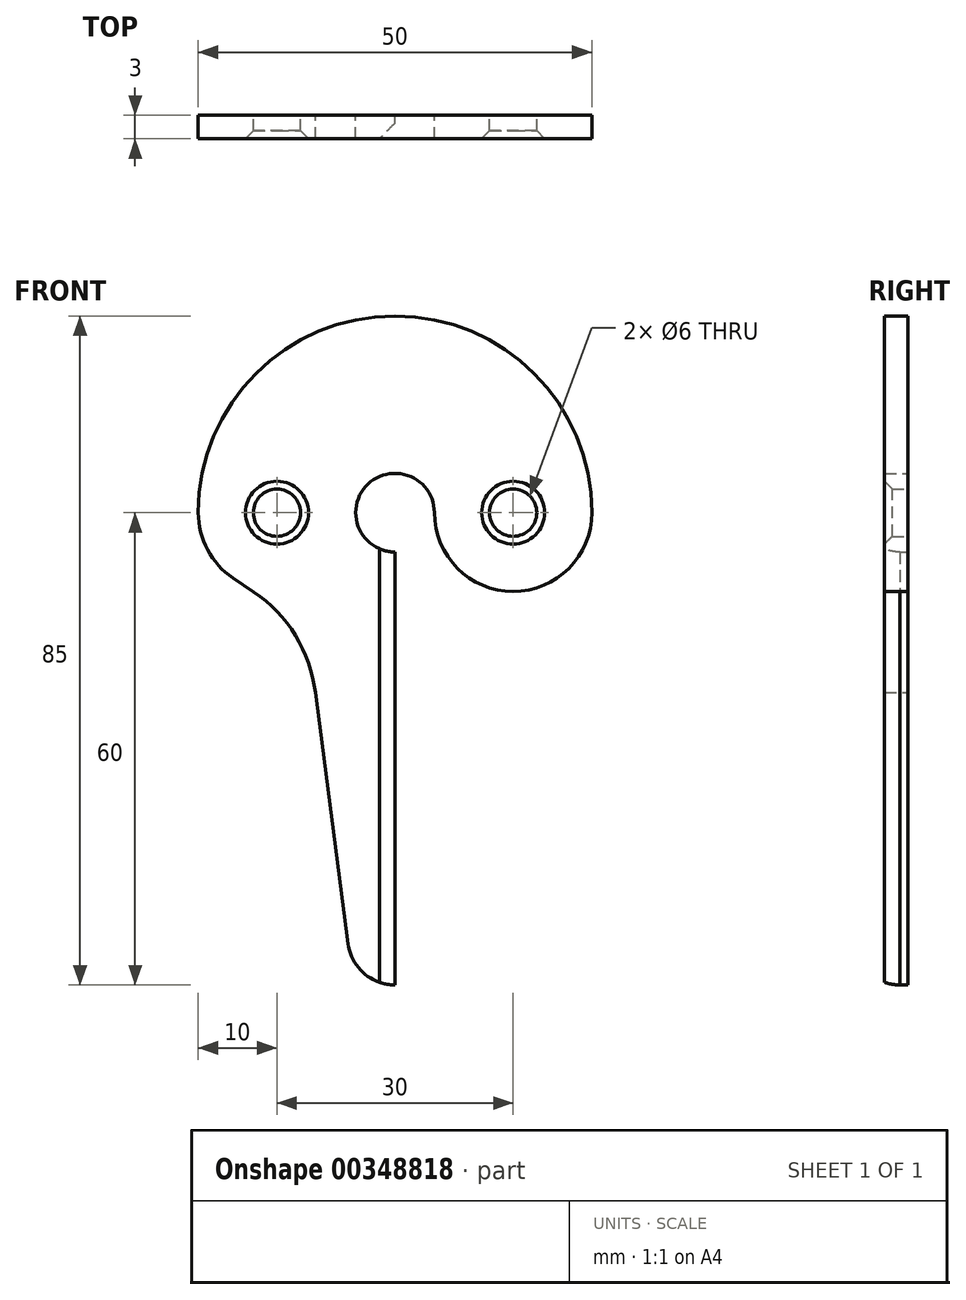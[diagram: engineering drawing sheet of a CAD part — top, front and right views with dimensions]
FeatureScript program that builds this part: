
annotation { "Feature Type Name" : "Feature", "Feature Type Description" : "" }
export const myFeature = defineFeature(function(context is Context, id is Id, definition is map)
    precondition{}
    {
        {
            var Q0;
            Q0=qCreatedBy(makeId("Front.planeOp"),FACE);
            var sketch = newSketch(context, id + "F0", { "sketchPlane" : qUnion([Q0])});
            skArc(sketch, "E0", {"start": v(5, 0) * mm, "mid": v(-3.54, 3.54) * mm, "end": v(0, -5) * mm});
            skArc(sketch, "E1", {"start": v(25, 0) * mm, "mid": v(0, 25) * mm, "end": v(-25, 0) * mm});
            skPoint(sketch, "E2", {"position": v(15, 0) * mm});
            skPoint(sketch, "E3", {"position": v(0, -54) * mm});
            skPoint(sketch, "E4", {"position": v(-28, -25) * mm});
            skCircle(sketch, "E5", {"center": v(15, 0) * mm, "radius": 3 * mm});
            skArc(sketch, "E6", {"start": v(5, 0) * mm, "mid": v(15, -10) * mm, "end": v(25, 0) * mm});
            skPoint(sketch, "E7.MirrorP", {"position": v(-15, 0) * mm});
            skCircle(sketch, "E8.MirrorC", {"center": v(-15, 0) * mm, "radius": 3 * mm});
            skArc(sketch, "E9.MirrorC", {"start": v(-20.58, -8.3) * mm, "mid": v(-23.83, -4.7) * mm, "end": v(-25, 0) * mm});
            skArc(sketch, "E10", {"start": v(-10.13, -22.86) * mm, "mid": v(-12.65, -15.6) * mm, "end": v(-17.96, -10.06) * mm});
            skArc(sketch, "E11", {"start": v(-5.95, -54.78) * mm, "mid": v(-3.96, -58.5) * mm, "end": v(0, -60) * mm});
            skLineSegment(sketch, "E12", {"start": v(0, 0) * mm, "end": v(0, -60) * mm});
            skLineSegment(sketch, "E13", {"start": v(-5.95, -54.78) * mm, "end": v(-10.15, -22.66) * mm});
            skArc(sketch, "E14.trimOffspring", {"start": v(-10.13, -22.86) * mm, "mid": v(-10.13, -22.86) * mm, "end": v(-10.13, -22.86) * mm});
            skLineSegment(sketch, "E15", {"start": v(-17.96, -10.06) * mm, "end": v(-20.58, -8.3) * mm});
            skSolve(sketch);
        }
        {
            var Q0;
            Q0 = qSketchRegion(id + "F0", true);
            extrude(context, id + "F1", {"entities" : qUnion([Q0]), "depth" : 3 * mm});
        }
        {
            var Q0;
            Q0=makeQuery(id+"F1.opExtrude","CAP_EDGE",EDGE,{"disambiguationData":[OSD([sQuery(id+"F0.wireOp",EDGE,"E8.MirrorC")])],"isStart":false});
            var Q1;
            Q1=makeQuery(id+"F1.opExtrude","CAP_EDGE",EDGE,{"disambiguationData":[OSD([sQuery(id+"F0.wireOp",EDGE,"E5")])],"isStart":false});
            chamfer(context, id + "F2", {"entities" : qUnion([Q0, Q1]), "width" : 1 * mm, "tangentPropagation" : true});
        }
        {
            var Q0;
            Q0=makeQuery(id+"F1.opExtrude","CAP_EDGE",EDGE,{"disambiguationData":[OSD([sQuery(id+"F0.wireOp",EDGE,"E12")])],"isStart":false});
            chamfer(context, id + "F3", {"entities" : qUnion([Q0]), "width" : 2 * mm, "tangentPropagation" : true});
        }
    });
